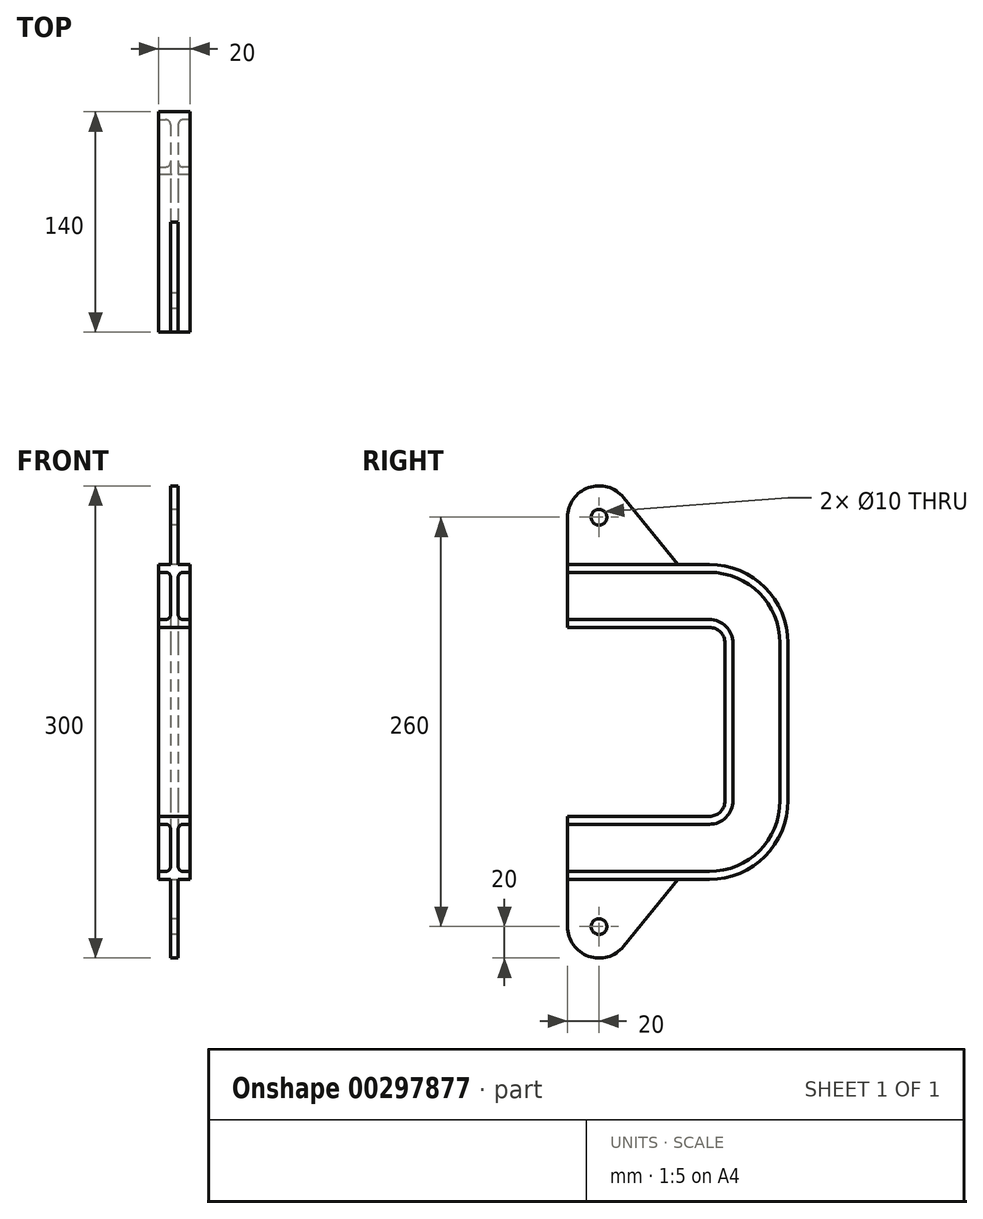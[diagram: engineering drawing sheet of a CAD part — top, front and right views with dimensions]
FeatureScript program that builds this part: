
annotation { "Feature Type Name" : "Feature", "Feature Type Description" : "" }
export const myFeature = defineFeature(function(context is Context, id is Id, definition is map)
    precondition{}
    {
        {
            var Q0;
            Q0=qCreatedBy(makeId("Front.planeOp"),FACE);
            var sketch = newSketch(context, id + "F0", { "sketchPlane" : qUnion([Q0])});
            skLineSegment(sketch, "E0", {"start": v(0, 20) * mm, "end": v(10, 20) * mm});
            skLineSegment(sketch, "E1", {"start": v(10, 20) * mm, "end": v(10, 15) * mm});
            skLineSegment(sketch, "E2", {"start": v(10, 15) * mm, "end": v(5.5, 15) * mm});
            skLineSegment(sketch, "E3", {"start": v(2.5, 12) * mm, "end": v(2.5, 0) * mm});
            skPoint(sketch, "E4.visualSharp", {"position": v(2.5, 15) * mm});
            skArc(sketch, "E4.filletArc", {"start": v(5.5, 15) * mm, "mid": v(3.38, 14.12) * mm, "end": v(2.5, 12) * mm});
            skArc(sketch, "E5.MirrorCS", {"start": v(-5.5, 15) * mm, "mid": v(-3.38, 14.12) * mm, "end": v(-2.5, 12) * mm});
            skLineSegment(sketch, "E6.MirrorCS", {"start": v(-10, 15) * mm, "end": v(-5.5, 15) * mm});
            skLineSegment(sketch, "E7.MirrorCS", {"start": v(0, 20) * mm, "end": v(-10, 20) * mm});
            skLineSegment(sketch, "E8.MirrorCS", {"start": v(-2.5, 12) * mm, "end": v(-2.5, 0) * mm});
            skLineSegment(sketch, "E9.MirrorCS", {"start": v(-10, 20) * mm, "end": v(-10, 15) * mm});
            skPoint(sketch, "E10.MirrorP", {"position": v(-2.5, 15) * mm});
            skArc(sketch, "E11.MirrorCS", {"start": v(5.5, -15) * mm, "mid": v(3.38, -14.12) * mm, "end": v(2.5, -12) * mm});
            skArc(sketch, "E12.MirrorCS", {"start": v(-5.5, -15) * mm, "mid": v(-3.38, -14.12) * mm, "end": v(-2.5, -12) * mm});
            skLineSegment(sketch, "E13.MirrorCS", {"start": v(10, -15) * mm, "end": v(5.5, -15) * mm});
            skPoint(sketch, "E14.MirrorP", {"position": v(-2.5, -15) * mm});
            skLineSegment(sketch, "E15.MirrorCS", {"start": v(-10, -20) * mm, "end": v(-10, -15) * mm});
            skLineSegment(sketch, "E16.MirrorCS", {"start": v(-2.5, -12) * mm, "end": v(-2.5, 0) * mm});
            skLineSegment(sketch, "E17.MirrorCS", {"start": v(0, -20) * mm, "end": v(-10, -20) * mm});
            skLineSegment(sketch, "E18.MirrorCS", {"start": v(-10, -15) * mm, "end": v(-5.5, -15) * mm});
            skLineSegment(sketch, "E19.MirrorCS", {"start": v(10, -20) * mm, "end": v(10, -15) * mm});
            skPoint(sketch, "E20.MirrorP", {"position": v(2.5, -15) * mm});
            skLineSegment(sketch, "E21.MirrorCS", {"start": v(0, -20) * mm, "end": v(10, -20) * mm});
            skLineSegment(sketch, "E22.MirrorCS", {"start": v(2.5, -12) * mm, "end": v(2.5, 0) * mm});
            skSolve(sketch);
        }
        {
            var Q0;
            Q0=qCreatedBy(makeId("Right.planeOp"),FACE);
            var sketch = newSketch(context, id + "F1", { "sketchPlane" : qUnion([Q0])});
            skLineSegment(sketch, "E23", {"start": v(0, -20) * mm, "end": v(90, -20) * mm});
            skLineSegment(sketch, "E24", {"start": v(100, -30) * mm, "end": v(100, -80) * mm});
            skPoint(sketch, "E25.visualSharp", {"position": v(100, -20) * mm});
            skArc(sketch, "E25.filletArc", {"start": v(100, -30) * mm, "mid": v(97.07, -22.93) * mm, "end": v(90, -20) * mm});
            skLineSegment(sketch, "E26", {"start": v(49.57, -80) * mm, "end": v(157.12, -80) * mm, "construction": true});
            skArc(sketch, "E27.MirrorCS", {"start": v(100, -130) * mm, "mid": v(97.07, -137.07) * mm, "end": v(90, -140) * mm});
            skLineSegment(sketch, "E28.MirrorCS", {"start": v(100, -130) * mm, "end": v(100, -80) * mm});
            skLineSegment(sketch, "E29.MirrorCS", {"start": v(0, -140) * mm, "end": v(90, -140) * mm});
            skPoint(sketch, "E30.MirrorP", {"position": v(100, -140) * mm});
            skSolve(sketch);
        }
        {
            var Q0;
            Q0 = qSketchRegion(id + "F0", true);
            var Q1;
            Q1=sQuery(id+"F1.wireOp",EDGE,"E23");
            var Q2;
            Q2=sQuery(id+"F1.wireOp",EDGE,"E25.filletArc");
            var Q3;
            Q3=sQuery(id+"F1.wireOp",EDGE,"E24");
            var Q4;
            Q4=sQuery(id+"F1.wireOp",EDGE,"E28.MirrorCS");
            var Q5;
            Q5=sQuery(id+"F1.wireOp",EDGE,"E27.MirrorCS");
            var Q6;
            Q6=sQuery(id+"F1.wireOp",EDGE,"E29.MirrorCS");
            sweep(context, id + "F2", {"profiles" : qUnion([Q0]), "path" : qUnion([Q1, Q2, Q3, Q4, Q5, Q6])});
        }
        {
            var Q0;
            Q0=qCreatedBy(makeId("Right.planeOp"),FACE);
            var sketch = newSketch(context, id + "F3", { "sketchPlane" : qUnion([Q0])});
            skLineSegment(sketch, "E31", {"start": v(0, 20) * mm, "end": v(70, 20) * mm});
            skLineSegment(sketch, "E32", {"start": v(70, 20) * mm, "end": v(35.55, 62.58) * mm});
            skArc(sketch, "E33", {"start": v(35.55, 62.58) * mm, "mid": v(13.33, 68.85) * mm, "end": v(0, 50) * mm});
            skLineSegment(sketch, "E34", {"start": v(0, 50) * mm, "end": v(0, 20) * mm});
            skCircle(sketch, "E35", {"center": v(20, 50) * mm, "radius": 5 * mm});
            skLineSegment(sketch, "E36", {"start": v(0, -80) * mm, "end": v(193.22, -80) * mm});
            skLineSegment(sketch, "E37.MirrorCS", {"start": v(0, -180) * mm, "end": v(70, -180) * mm});
            skLineSegment(sketch, "E38.MirrorCS", {"start": v(0, -210) * mm, "end": v(0, -180) * mm});
            skLineSegment(sketch, "E39.MirrorCS", {"start": v(70, -180) * mm, "end": v(35.55, -222.58) * mm});
            skCircle(sketch, "E40.MirrorC", {"center": v(20, -210) * mm, "radius": 5 * mm});
            skArc(sketch, "E41.MirrorCS", {"start": v(35.55, -222.58) * mm, "mid": v(13.33, -228.85) * mm, "end": v(0, -210) * mm});
            skSolve(sketch);
        }
        {
            var Q0;
            Q0 = qSketchRegion(id + "F3", true);
            extrude(context, id + "F4", {"entities" : qUnion([Q0]), "operationType" : NewBodyOperationType.ADD, "endBound" : BoundingType.SYMMETRIC, "depth" : 5 * mm});
        }
    });
